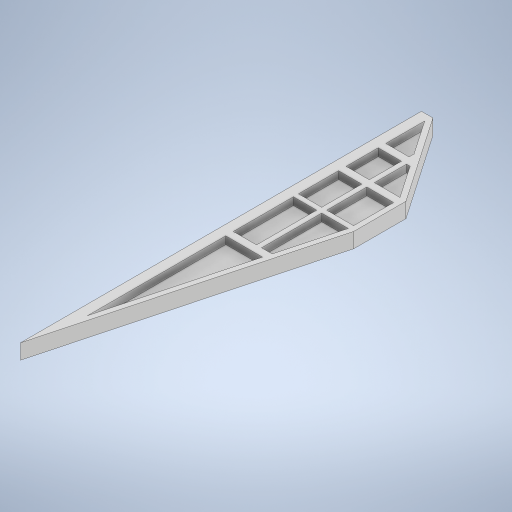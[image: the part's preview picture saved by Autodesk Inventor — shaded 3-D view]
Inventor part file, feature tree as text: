
AUTODESK INVENTOR PART (.ipt)
format: ipt  version: 2024 (Build 280153000, 153)  size: 295,424 bytes
history: native  units: in
note: dims shown in document units (in); Inventor stores cm internally (conversion verified against a paired STEP export)
features: other x3, sketch x2
ambient origin geometry x8: Origin, YZ Plane, XZ Plane, XY Plane, X Axis, Y Axis, Z Axis, Center Point
bodies: Solid1 (feature_tree)
feature tree (5):
  other  "Nozki.ipt"
  other  "Solid1::Nozki.ipt"
  other  "TaggingFeature1"
  sketch  "Sketch1"  dims[d0=0.3937in]
  sketch  "Sketch2"
